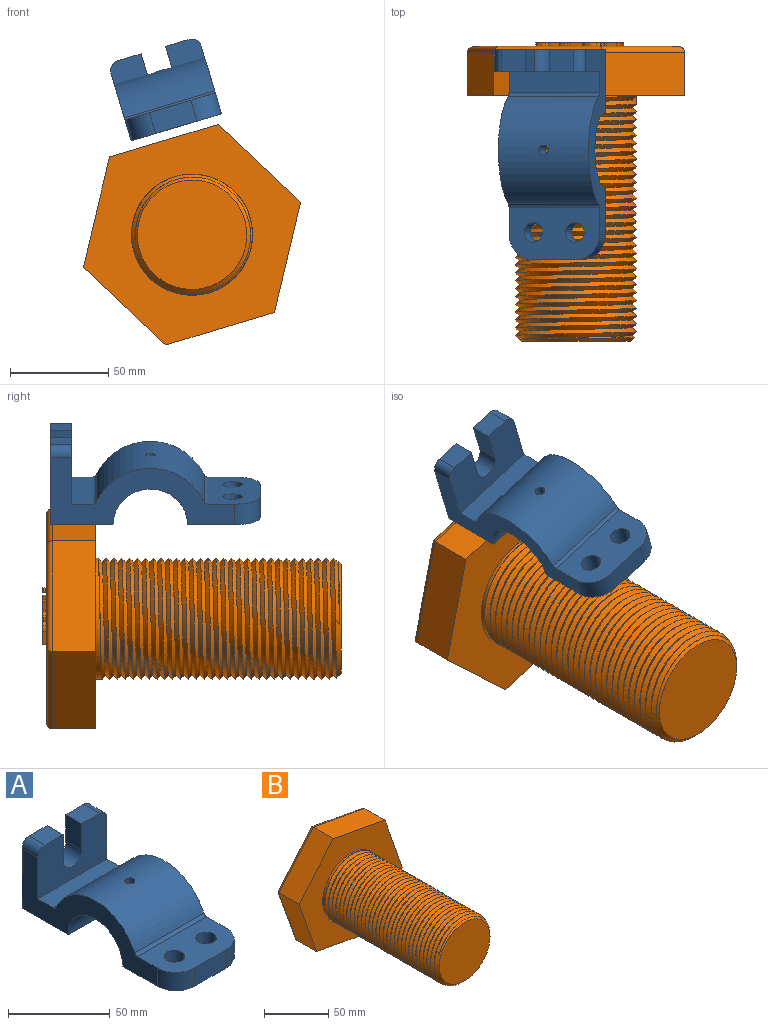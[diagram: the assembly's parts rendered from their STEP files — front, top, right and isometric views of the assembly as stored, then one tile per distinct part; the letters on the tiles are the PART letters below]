
ASSEMBLY  parts=2 mates=1
PART A: 25 faces, bbox 48x107x41 mm
  f0: cylinder r=19mm len=48mm, axis (-1,0,0), area 2845.5mm2, adj f4,f5,f11,f12,f18
  f1: cylinder r=30mm len=54.83mm, axis (-1,0,0), area 3299.4mm2, adj f11,f12,f18,f23,f24
  f2: plane 12.5x11mm, normal (0,0,1), area 137.5mm2, adj f3,f7,f15,f22
  f3: plane 48x41mm, normal (0,1,0), area 1682.9mm2, adj f2,f5,f6,f11,f12,f13,f14,f15
  f4: plane 48x37mm, normal (0,0,-1), area 1546.4mm2, adj f0,f10,f11,f12,f16,f17,f19,f20
  f5: plane 48x32mm, normal (0,0,-1), area 1536mm2, adj f0,f3,f11,f12
  f6: plane 12.5x11mm, normal (0,0,1), area 137.5mm2, adj f3,f7,f14,f21
  f7: plane 48x30mm, normal (0,-1,0), area 1154.9mm2, adj f2,f6,f8,f11,f12,f13,f14,f15
  f8: plane 48x10.76mm, normal (0,0,1), area 516.5mm2, adj f7,f11,f12,f24
  f9: plane 48x26.76mm, normal (0,0,1), area 1054.8mm2, adj f10,f11,f12,f16,f17,f19,f20,f23
  f10: plane 22x11mm, normal (0,-1,0), area 242mm2, adj f4,f9,f19,f20
  f11: plane 94x36mm, normal (1,0,0), area 1511.4mm2, adj f0,f1,f3,f4,f5,f7,f8,f9
  f12: plane 94x36mm, normal (-1,0,0), area 1511.4mm2, adj f0,f1,f3,f4,f5,f7,f8,f9
  f13: cylinder r=6.5mm len=13mm, axis (0,1,0), area 224.6mm2, adj f3,f7,f14,f15
  f14: plane 16x11mm, normal (1,0,0), area 176mm2, adj f3,f6,f7,f13
  f15: plane 16x11mm, normal (-1,0,0), area 176mm2, adj f2,f3,f7,f13
  f16: cylinder r=5mm len=11mm, axis (0,0,-1), area 345.6mm2, adj f4,f9
  f17: cylinder r=5mm len=11mm, axis (0,0,-1), area 345.6mm2, adj f4,f9
  f18: cylinder r=2.5mm len=11.17mm, axis (0,0,-1), area 173.3mm2, adj f0,f1
  f19: cylinder r=13mm len=13mm, axis (0,0,-1), area 224.6mm2, adj f4,f9,f10,f12
  f20: cylinder r=13mm len=13mm, axis (0,0,1), area 224.6mm2, adj f4,f9,f10,f11
  f21: cylinder r=5mm len=11mm, axis (0,-1,0), area 86.4mm2, adj f3,f6,f7,f12
  f22: cylinder r=5mm len=11mm, axis (0,1,0), area 86.4mm2, adj f2,f3,f7,f11
  f23: cylinder r=2mm len=48mm, axis (-1,0,0), area 110.6mm2, adj f1,f9,f11,f12
  f24: cylinder r=2mm len=48mm, axis (-1,0,0), area 110.6mm2, adj f1,f8,f11,f12
PART B: 96 faces, bbox 113.5x153.6x108.9 mm
  f0: plane 106.71x102.34mm, normal (0,1,0), area 7423.7mm2, adj f15,f16,f17,f18,f19,f20,f21,f22
  f1: cylinder r=30.86mm len=61.72mm, axis (0,1,0), area 444.9mm2, adj f2,f3,f14
  f2: plane 4.08x1.86mm, normal (0.39,0,0.92), area 4.2mm2, adj f1,f3,f4,f5
  f3: bspline ~61.66x61.61mm, area 19.3mm2, adj f1,f2,f4
  f4: bspline ~123.91x61.55mm, area 15493.7mm2, adj f2,f3,f5,f7
  f5: bspline ~124.78x71.11mm, area 16198.1mm2, adj f2,f4,f7
  f6: plane 55.72x55.72mm, normal (0,-1,0), area 2438.7mm2, adj f7
  f7: cone r=27.86mm half-angle=45deg, axis (0,1,0), area 502.7mm2, adj f4,f5,f6
  f8: plane 56.76x22mm, normal (0.18,0,0.98), area 1270.2mm2, adj f9,f13,f14,f17
  f9: plane 43.88x37.52mm, normal (-0.76,0,0.65), area 1270.2mm2, adj f8,f10,f14,f15
  f10: plane 54.44x22mm, normal (-0.94,0,-0.33), area 1270.2mm2, adj f9,f11,f14,f16
  f11: plane 56.76x22mm, normal (-0.18,0,-0.98), area 1270.2mm2, adj f10,f12,f14,f18
  f12: plane 43.88x37.52mm, normal (0.76,0,-0.65), area 1270.2mm2, adj f11,f13,f14,f20
  f13: plane 54.44x22mm, normal (0.94,0,0.33), area 1270.2mm2, adj f8,f12,f14,f19
  f14: plane 113.52x108.87mm, normal (0,-1,0), area 5668.1mm2, adj f1,f8,f9,f10,f11,f12,f13
  f15: cylinder r=3mm len=45.83mm, axis (0.65,0,0.76), area 263.9mm2, adj f0,f9,f16,f17
  f16: cylinder r=3mm len=55.44mm, axis (-0.33,0,0.94), area 263.9mm2, adj f0,f10,f15,f18
  f17: cylinder r=3mm len=57.31mm, axis (0.98,0,-0.18), area 263.9mm2, adj f0,f8,f15,f19
  f18: cylinder r=3mm len=57.31mm, axis (-0.98,0,0.18), area 263.9mm2, adj f0,f11,f16,f20
  f19: cylinder r=3mm len=55.44mm, axis (0.33,0,-0.94), area 263.9mm2, adj f0,f13,f17,f20
  f20: cylinder r=3mm len=45.83mm, axis (-0.65,0,-0.76), area 263.9mm2, adj f0,f12,f18,f19
  f21: extruded ~2x1.58mm, area 3.2mm2, adj f0,f22,f29,f30
  f22: extruded ~3.55x2.77mm, area 10.3mm2, adj f0,f21,f23,f30
  f23: plane 12.81x2mm, normal (-1,0,0.09), area 25.7mm2, adj f0,f22,f24,f30
  f24: plane 2x1.68mm, normal (0.09,0,1), area 3.4mm2, adj f0,f23,f25,f30
  f25: plane 12.93x2mm, normal (1,0,-0.09), area 26mm2, adj f0,f24,f26,f30
  f26: extruded ~2x1.34mm, area 2.8mm2, adj f0,f25,f27,f30
  f27: extruded ~2x1.12mm, area 2.6mm2, adj f0,f26,f28,f30
  f28: extruded ~2x1.4mm, area 2.8mm2, adj f0,f27,f29,f30
  f29: plane 2x1.37mm, normal (1,0,-0.09), area 2.7mm2, adj f0,f21,f28,f30
  f30: plane 16.43x4.73mm, normal (0,1,0), area 30.2mm2, adj f21,f22,f23,f24,f25,f26,f27,f28
  f31: extruded ~2x0.87mm, area 1.8mm2, adj f0,f32,f38,f39
  f32: extruded ~2x0.82mm, area 1.8mm2, adj f0,f31,f33,f39
  f33: extruded ~2x0.74mm, area 1.6mm2, adj f0,f32,f34,f39
  f34: extruded ~2x0.67mm, area 1.5mm2, adj f0,f33,f35,f39
  f35: extruded ~2x0.87mm, area 1.8mm2, adj f0,f34,f36,f39
  f36: extruded ~2x0.82mm, area 1.8mm2, adj f0,f35,f37,f39
  f37: extruded ~2x0.72mm, area 1.5mm2, adj f0,f36,f38,f39
  f38: extruded ~2x0.69mm, area 1.6mm2, adj f0,f31,f37,f39
  f39: plane 2.3x2.08mm, normal (0,1,0), area 3.7mm2, adj f31,f32,f33,f34,f35,f36,f37,f38
  f40: extruded ~3.17x2mm, area 6.9mm2, adj f41,f56,f57,f58
  f41: extruded ~3.31x2mm, area 6.8mm2, adj f40,f42,f57,f58
  f42: extruded ~2.4x2mm, area 5.7mm2, adj f41,f43,f57,f58
  f43: extruded ~2.63x2mm, area 5.7mm2, adj f42,f44,f57,f58
  f44: extruded ~3.14x2mm, area 6.8mm2, adj f43,f45,f57,f58
  f45: extruded ~3.32x2mm, area 6.9mm2, adj f44,f46,f57,f58
  f46: extruded ~2.41x2mm, area 5.7mm2, adj f45,f56,f57,f58
  f47: extruded ~4.36x2mm, area 9.2mm2, adj f0,f48,f55,f57
  f48: extruded ~4.07x2mm, area 9.1mm2, adj f0,f47,f49,f57
  f49: extruded ~3.84x2mm, area 8.3mm2, adj f0,f48,f50,f57
  f50: extruded ~3.64x2mm, area 8.4mm2, adj f0,f49,f51,f57
  f51: extruded ~4.35x2mm, area 9.1mm2, adj f0,f50,f52,f57
  f52: extruded ~3.01x2mm, area 6.3mm2, adj f0,f51,f53,f57
  f53: extruded ~2x1.96mm, area 5.5mm2, adj f0,f52,f54,f57
  f54: extruded ~2.71x2mm, area 5.6mm2, adj f0,f53,f55,f57
  f55: extruded ~3.65x2mm, area 8.4mm2, adj f0,f47,f54,f57
  f56: extruded ~2.6x2mm, area 5.7mm2, adj f40,f46,f57,f58
  f57: plane 11.79x10.6mm, normal (0,1,0), area 47.7mm2, adj f40,f41,f42,f43,f44,f45,f46,f47
  f58: plane 8.93x7.04mm, normal (0,1,0), area 48.7mm2, adj f40,f41,f42,f43,f44,f45,f46,f56
  f59: plane 7.19x2mm, normal (1,0,-0.09), area 14.4mm2, adj f0,f60,f76,f77
  f60: plane 2x1.68mm, normal (-0.09,0,-1), area 3.4mm2, adj f0,f59,f61,f77
  f61: plane 7.24x2mm, normal (-1,0,0.09), area 14.5mm2, adj f0,f60,f62,f77
  f62: extruded ~2.99x2mm, area 6.7mm2, adj f0,f61,f63,f77
  f63: extruded ~3.14x2mm, area 6.6mm2, adj f0,f62,f64,f77
  f64: extruded ~2.05x2mm, area 4.3mm2, adj f0,f63,f65,f77
  f65: extruded ~2x1.39mm, area 3.9mm2, adj f0,f64,f66,f77
  f66: plane 2x0.1mm, normal (0.09,0,1), area 0.2mm2, adj f0,f65,f67,f77
  f67: extruded ~2x1.44mm, area 2.9mm2, adj f0,f66,f68,f77
  f68: plane 4.77x2mm, normal (-1,0,0.09), area 9.6mm2, adj f0,f67,f69,f77
  f69: plane 2x1.68mm, normal (0.09,0,1), area 3.4mm2, adj f0,f68,f70,f77
  f70: plane 15.77x2mm, normal (1,0,-0.09), area 31.7mm2, adj f0,f69,f71,f77
  f71: plane 2x1.68mm, normal (-0.09,0,-1), area 3.4mm2, adj f0,f70,f72,f77
  f72: plane 5.81x2mm, normal (-1,0,0.09), area 11.7mm2, adj f0,f71,f73,f77
  f73: extruded ~3.19x2mm, area 6.6mm2, adj f0,f72,f74,f77
  f74: extruded ~2.47x2mm, area 5.7mm2, adj f0,f73,f75,f77
  f75: extruded ~2x2mm, area 4.2mm2, adj f0,f74,f76,f77
  f76: extruded ~2x1.97mm, area 4.4mm2, adj f0,f59,f75,f77
  f77: plane 15.92x10.67mm, normal (0,1,0), area 53.1mm2, adj f59,f60,f61,f62,f63,f64,f65,f66
  f78: plane 7.19x2mm, normal (1,0,-0.09), area 14.4mm2, adj f0,f79,f94,f95
  f79: plane 2x1.68mm, normal (-0.09,0,-1), area 3.4mm2, adj f0,f78,f80,f95
  f80: plane 7.24x2mm, normal (-1,0,0.09), area 14.5mm2, adj f0,f79,f81,f95
  f81: extruded ~3.01x2mm, area 6.7mm2, adj f0,f80,f82,f95
  f82: extruded ~3.11x2mm, area 6.5mm2, adj f0,f81,f83,f95
  f83: extruded ~2.04x2mm, area 4.3mm2, adj f0,f82,f84,f95
  f84: extruded ~2x1.4mm, area 3.9mm2, adj f0,f83,f85,f95
  f85: plane 2x0.08mm, normal (0.09,0,1), area 0.2mm2, adj f0,f84,f86,f95
  f86: plane 2x1.5mm, normal (-0.97,0,0.26), area 3.1mm2, adj f0,f85,f87,f95
  f87: plane 2x1.37mm, normal (0.09,0,1), area 2.7mm2, adj f0,f86,f88,f95
  f88: plane 11.11x2mm, normal (1,0,-0.09), area 22.3mm2, adj f0,f87,f89,f95
  f89: plane 2x1.68mm, normal (-0.09,0,-1), area 3.4mm2, adj f0,f88,f90,f95
  f90: plane 5.83x2mm, normal (-1,0,0.09), area 11.7mm2, adj f0,f89,f91,f95
  f91: extruded ~3.18x2mm, area 6.6mm2, adj f0,f90,f92,f95
  f92: extruded ~2.47x2mm, area 5.6mm2, adj f0,f91,f93,f95
  f93: extruded ~2x2mm, area 4.2mm2, adj f0,f92,f94,f95
  f94: extruded ~2x1.97mm, area 4.4mm2, adj f0,f78,f93,f95
  f95: plane 11.92x10.26mm, normal (0,1,0), area 45.1mm2, adj f78,f79,f80,f81,f82,f83,f84,f85
PLACE A rot(axis=(0,-1,0),16.7deg) t=(28.49,139.68,16.13)mm
PLACE B rot(axis=(0,-1,0),27.2deg) t=(36.46,167.54,-38.62)mm
MATE parallel B.f8 <-> A.f5  axis (-0.29,0,0.96) through (22.12,178.54,9.28)mm
